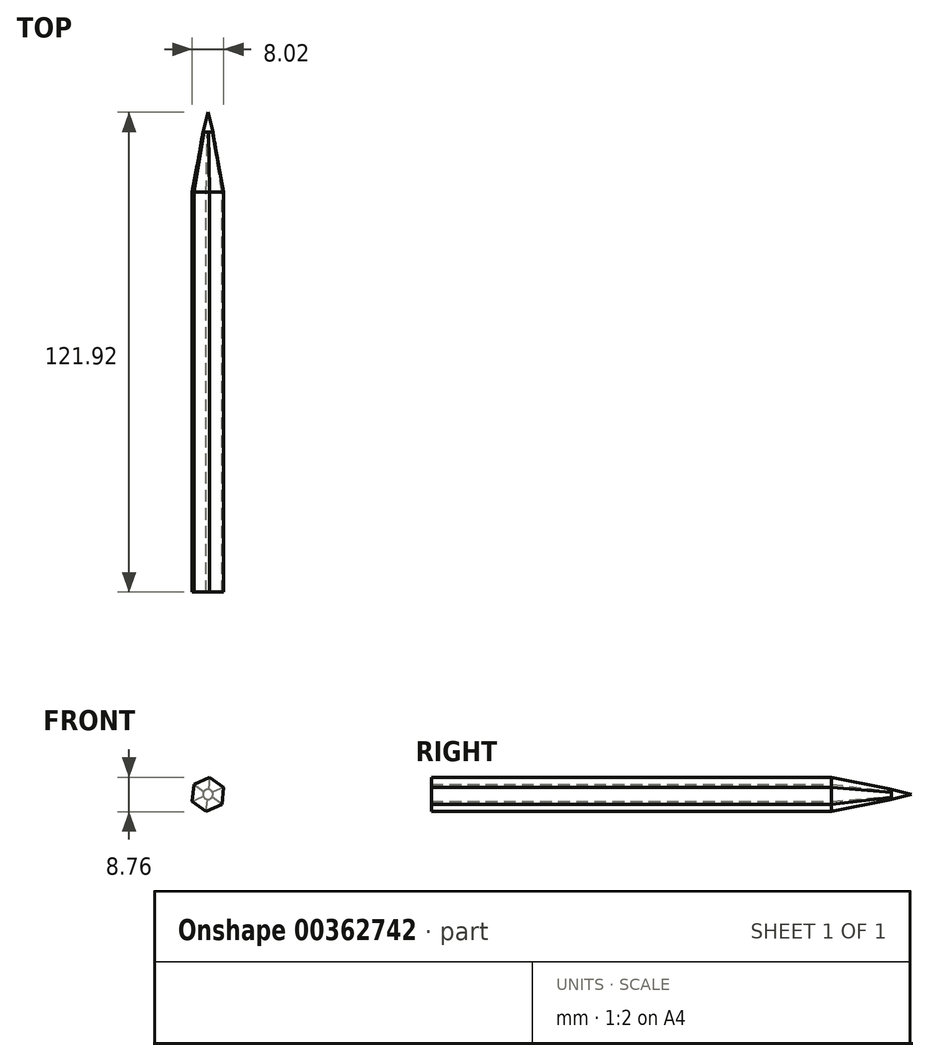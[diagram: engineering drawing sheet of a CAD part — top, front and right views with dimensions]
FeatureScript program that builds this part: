
annotation { "Feature Type Name" : "Feature", "Feature Type Description" : "" }
export const myFeature = defineFeature(function(context is Context, id is Id, definition is map)
    precondition{}
    {
        {
            var Q0;
            Q0=qCreatedBy(makeId("Front.planeOp"),FACE);
            var sketch = newSketch(context, id + "F0", { "sketchPlane" : qUnion([Q0])});
            skCircle(sketch, "E0.cCircle", {"center": v(0, 0) * mm, "radius": 4.4 * mm, "construction": true});
            skLineSegment(sketch, "E0.0", {"start": v(-3.57, 2.58) * mm, "end": v(0.45, 4.38) * mm});
            skLineSegment(sketch, "E0.1", {"start": v(0.45, 4.38) * mm, "end": v(4.01, 1.8) * mm});
            skLineSegment(sketch, "E0.2", {"start": v(4.01, 1.8) * mm, "end": v(3.57, -2.58) * mm});
            skLineSegment(sketch, "E0.3", {"start": v(3.57, -2.58) * mm, "end": v(-0.45, -4.38) * mm});
            skLineSegment(sketch, "E0.4", {"start": v(-0.45, -4.38) * mm, "end": v(-4.01, -1.8) * mm});
            skLineSegment(sketch, "E0.5", {"start": v(-4.01, -1.8) * mm, "end": v(-3.57, 2.58) * mm});
            skSolve(sketch);
        }
        {
            var Q0;
            Q0=makeQuery(id+"F0.imprint","IMPRINT",FACE,{"disambiguationData":[TD([[makeQuery(id+"F0.imprint","IMPRINT",EDGE,{"derivedFrom":sQuery(id+"F0.wireOp",EDGE,"E0.0")}),-1.0]])]});
            extrude(context, id + "F1", {"entities" : qUnion([Q0]), "endBound" : BoundingType.SYMMETRIC, "depth" : 101.6 * mm});
        }
        {
            var Q0;
            Q0=makeQuery(id+"F1.opExtrude","CAP_FACE",FACE,{"disambiguationData":[OSD([sQuery(id+"F0.wireOp",EDGE,"E0.0"),sQuery(id+"F0.wireOp",EDGE,"E0.1"),sQuery(id+"F0.wireOp",EDGE,"E0.2"),sQuery(id+"F0.wireOp",EDGE,"E0.3"),sQuery(id+"F0.wireOp",EDGE,"E0.4"),sQuery(id+"F0.wireOp",EDGE,"E0.5")])],"isStart":true});
            cPlane(context, id + "F2", {"entities" : qUnion([Q0]), "cplaneType" : CPlaneType.OFFSET, "offset" : 15.24 * mm, "width" : 152.4 * mm, "height" : 152.4 * mm});
        }
        {
            var Q0;
            Q0=qCreatedBy(id+"F2.planeOp",FACE);
            var sketch = newSketch(context, id + "F3", { "sketchPlane" : qUnion([Q0])});
            skCircle(sketch, "E1", {"center": v(0, 0) * mm, "radius": 1.27 * mm});
            skSolve(sketch);
        }
        {
            var Q1;
            Q1=makeQuery(id+"F1.opExtrude","CAP_FACE",FACE,{"disambiguationData":[OSD([sQuery(id+"F0.wireOp",EDGE,"E0.0"),sQuery(id+"F0.wireOp",EDGE,"E0.1"),sQuery(id+"F0.wireOp",EDGE,"E0.2"),sQuery(id+"F0.wireOp",EDGE,"E0.3"),sQuery(id+"F0.wireOp",EDGE,"E0.4"),sQuery(id+"F0.wireOp",EDGE,"E0.5")])],"isStart":true});
            var Q2;
            Q2=makeQuery(id+"F3.imprint","IMPRINT",FACE,{"disambiguationData":[TD([[makeQuery(id+"F3.imprint","IMPRINT",EDGE,{"derivedFrom":sQuery(id+"F3.wireOp",EDGE,"E1")}),1.0]])]});
            loft(context, id + "F4", {"operationType" : NewBodyOperationType.ADD, "sheetProfilesArray" : [{ "sheetProfileEntities" : qUnion([Q1]) }, { "sheetProfileEntities" : qUnion([Q2]) }]});
        }
        {
            var Q0;
            Q0=makeQuery(id+"F4.opLoft","CAP_FACE",FACE,{"disambiguationData":[OSD([makeQuery(id+"F3.imprint","IMPRINT",FACE,{"disambiguationData":[TD([[makeQuery(id+"F3.imprint","IMPRINT",EDGE,{"derivedFrom":sQuery(id+"F3.wireOp",EDGE,"E1")}),1.0]])]})])],"isStart":true});
            cPlane(context, id + "F5", {"entities" : qUnion([Q0]), "cplaneType" : CPlaneType.OFFSET, "offset" : 5.08 * mm, "width" : 152.4 * mm, "height" : 152.4 * mm});
        }
        {
            var Q0;
            Q0=qCreatedBy(id+"F5.planeOp",FACE);
            var sketch = newSketch(context, id + "F6", { "sketchPlane" : qUnion([Q0])});
            skCircle(sketch, "E2", {"center": v(0, 0) * mm, "radius": 0.4 * mm});
            skSolve(sketch);
        }
        {
            var Q1;
            Q1=makeQuery(id+"F4.opLoft","CAP_FACE",FACE,{"disambiguationData":[OSD([makeQuery(id+"F3.imprint","IMPRINT",FACE,{"disambiguationData":[TD([[makeQuery(id+"F3.imprint","IMPRINT",EDGE,{"derivedFrom":sQuery(id+"F3.wireOp",EDGE,"E1")}),1.0]])]})])],"isStart":true});
            var Q2;
            Q2=sQuery(id+"F6.wireOp",VERTEX,"E2.center");
            loft(context, id + "F7", {"operationType" : NewBodyOperationType.ADD, "sheetProfilesArray" : [{ "sheetProfileEntities" : qUnion([Q1]) }, { "sheetProfileEntities" : qUnion([Q2]) }]});
        }
    });
